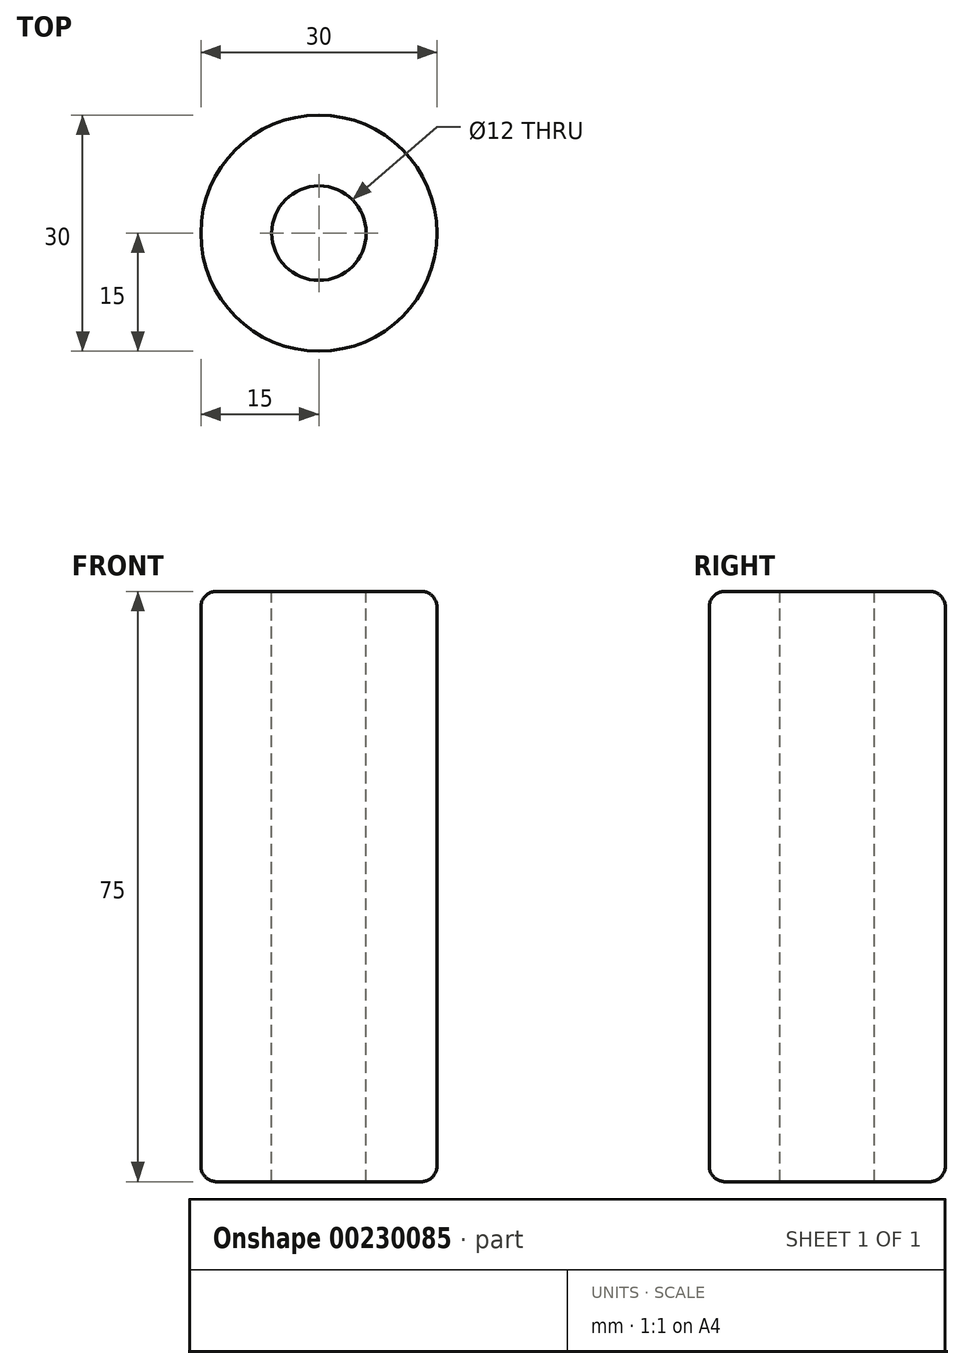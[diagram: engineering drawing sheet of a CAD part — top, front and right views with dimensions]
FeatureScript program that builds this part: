
annotation { "Feature Type Name" : "Feature", "Feature Type Description" : "" }
export const myFeature = defineFeature(function(context is Context, id is Id, definition is map)
    precondition{}
    {
        {
            var Q0;
            Q0=qCreatedBy(makeId("Top.planeOp"),FACE);
            var sketch = newSketch(context, id + "F0", { "sketchPlane" : qUnion([Q0])});
            skCircle(sketch, "E0", {"center": v(0, 0) * mm, "radius": 15 * mm});
            skSolve(sketch);
        }
        {
            var Q0;
            Q0=makeQuery(id+"F0.imprint","IMPRINT",FACE,{"disambiguationData":[TD([[makeQuery(id+"F0.imprint","IMPRINT",EDGE,{"derivedFrom":sQuery(id+"F0.wireOp",EDGE,"E0")}),1.0]])]});
            extrude(context, id + "F1", {"entities" : qUnion([Q0]), "endBound" : BoundingType.SYMMETRIC, "depth" : 75 * mm});
        }
        {
            var Q0;
            Q0=makeQuery(id+"F1.opExtrude","CAP_EDGE",EDGE,{"disambiguationData":[OSD([sQuery(id+"F0.wireOp",EDGE,"E0")])],"isStart":false});
            var Q1;
            Q1=makeQuery(id+"F1.opExtrude","CAP_EDGE",EDGE,{"disambiguationData":[OSD([sQuery(id+"F0.wireOp",EDGE,"E0")])],"isStart":true});
            fillet(context, id + "F2", {"entities" : qUnion([Q0, Q1]), "radius" : 2 * mm, "tangentPropagation" : true, "allowEdgeOverflow" : false});
        }
        {
            var Q0;
            Q0=makeQuery(id+"F1.opExtrude","CAP_FACE",FACE,{"disambiguationData":[OSD([sQuery(id+"F0.wireOp",EDGE,"E0")])],"isStart":false});
            var sketch = newSketch(context, id + "F3", { "sketchPlane" : qUnion([Q0])});
            skCircle(sketch, "E1", {"center": v(0, 0) * mm, "radius": 6 * mm});
            skSolve(sketch);
        }
        {
            var Q0;
            Q0=makeQuery(id+"F3.imprint","IMPRINT",FACE,{"disambiguationData":[TD([[makeQuery(id+"F3.imprint","IMPRINT",EDGE,{"derivedFrom":sQuery(id+"F3.wireOp",EDGE,"E1")}),1.0]])]});
            extrude(context, id + "F4", {"entities" : qUnion([Q0]), "operationType" : NewBodyOperationType.REMOVE, "endBound" : BoundingType.THROUGH_ALL, "oppositeDirection" : true, "depth" : 20 * mm});
        }
    });
